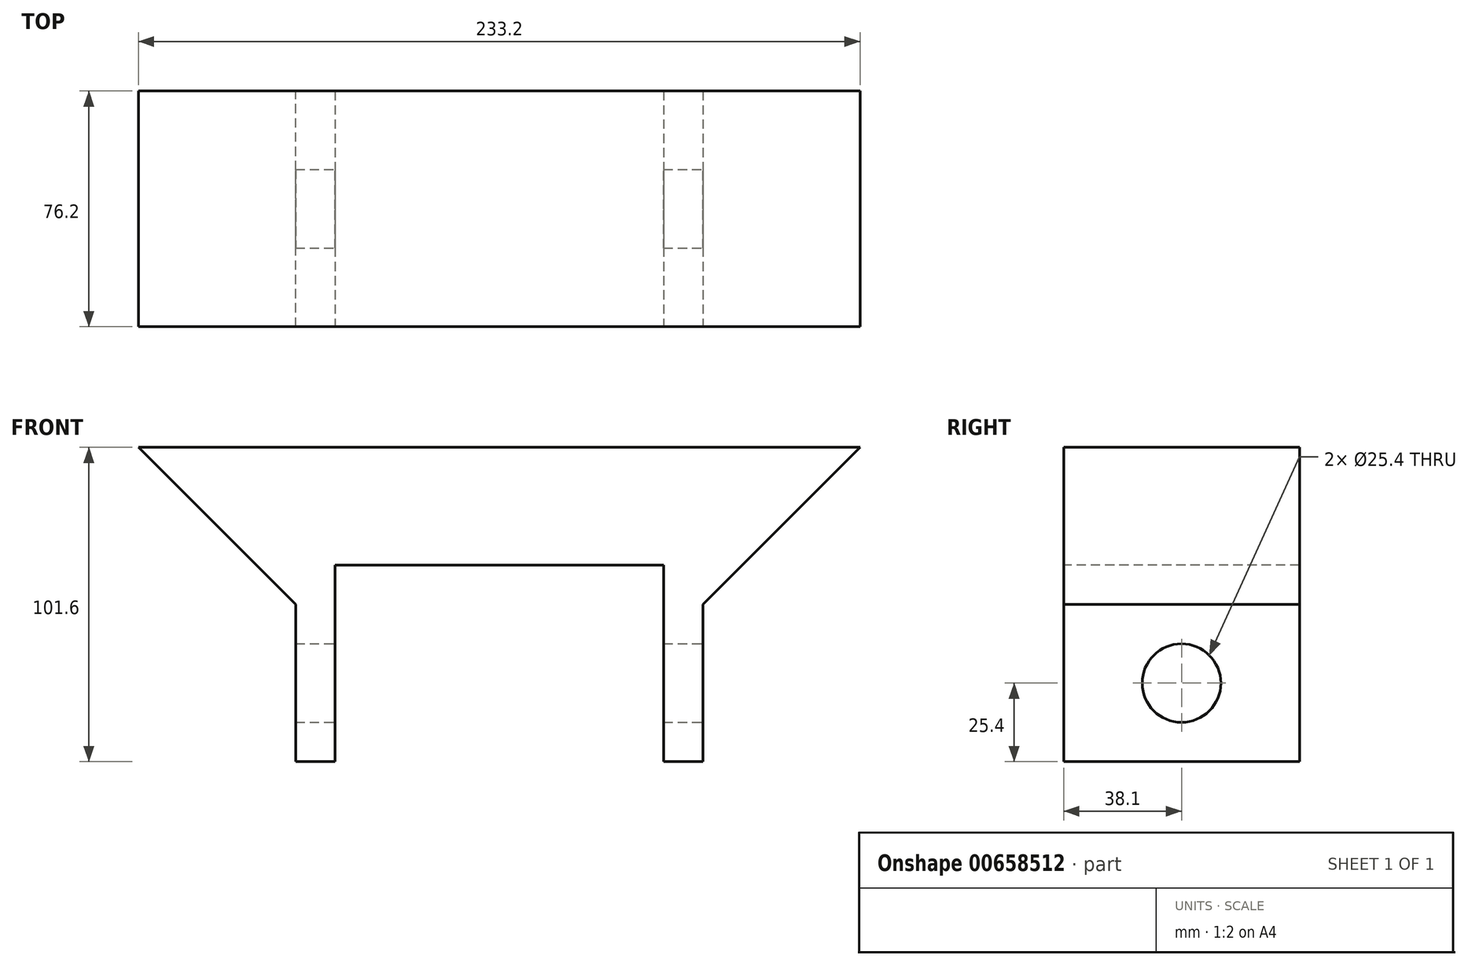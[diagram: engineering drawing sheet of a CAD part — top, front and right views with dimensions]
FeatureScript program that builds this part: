
annotation { "Feature Type Name" : "Feature", "Feature Type Description" : "" }
export const myFeature = defineFeature(function(context is Context, id is Id, definition is map)
    precondition{}
    {
        {
            var Q0;
            Q0=qCreatedBy(makeId("Top.planeOp"),FACE);
            var sketch = newSketch(context, id + "F0", { "sketchPlane" : qUnion([Q0])});
            skLineSegment(sketch, "E0.bottom", {"start": v(0, 0) * mm, "end": v(284, 0) * mm});
            skLineSegment(sketch, "E0.top", {"start": v(0, 76.2) * mm, "end": v(284, 76.2) * mm});
            skLineSegment(sketch, "E0.left", {"start": v(0, 0) * mm, "end": v(0, 76.2) * mm});
            skLineSegment(sketch, "E0.right", {"start": v(284, 0) * mm, "end": v(284, 76.2) * mm});
            skSolve(sketch);
        }
        {
            var Q0;
            Q0=makeQuery(id+"F0.imprint","IMPRINT",FACE,{"disambiguationData":[TD([[makeQuery(id+"F0.imprint","IMPRINT",EDGE,{"derivedFrom":sQuery(id+"F0.wireOp",EDGE,"E0.bottom")}),1.0]])]});
            extrude(context, id + "F1", {"entities" : qUnion([Q0]), "oppositeDirection" : true, "depth" : 50.8 * mm, "offsetDistance" : 25.4 * mm});
        }
        {
            var Q0;
            Q0=makeQuery(id+"F1.opExtrude","CAP_EDGE",EDGE,{"disambiguationData":[OSD([sQuery(id+"F0.wireOp",EDGE,"E0.left")])],"isStart":false});
            var Q1;
            Q1=makeQuery(id+"F1.opExtrude","CAP_EDGE",EDGE,{"disambiguationData":[OSD([sQuery(id+"F0.wireOp",EDGE,"E0.right")])],"isStart":false});
            chamfer(context, id + "F2", {"entities" : qUnion([Q0, Q1]), "width" : 76.2 * mm, "tangentPropagation" : true});
        }
        {
            var Q0;
            Q0=makeQuery(id+"F1.opExtrude","CAP_FACE",FACE,{"disambiguationData":[OSD([sQuery(id+"F0.wireOp",EDGE,"E0.bottom"),sQuery(id+"F0.wireOp",EDGE,"E0.top"),sQuery(id+"F0.wireOp",EDGE,"E0.left"),sQuery(id+"F0.wireOp",EDGE,"E0.right")])],"isStart":false});
            extrude(context, id + "F3", {"entities" : qUnion([Q0]), "operationType" : NewBodyOperationType.ADD, "depth" : 50.8 * mm, "offsetDistance" : 25.4 * mm});
        }
        {
            var Q0;
            Q0=makeQuery(id+"F3.opExtrude","CAP_FACE",FACE,{"disambiguationData":[OSD([sQuery(id+"F0.wireOp",EDGE,"E0.bottom"),sQuery(id+"F0.wireOp",EDGE,"E0.top"),sQuery(id+"F0.wireOp",EDGE,"E0.left"),sQuery(id+"F0.wireOp",EDGE,"E0.right")])],"isStart":false});
            var sketch = newSketch(context, id + "F4", { "sketchPlane" : qUnion([Q0])});
            skLineSegment(sketch, "E1.bottom", {"start": v(88.9, -76.2) * mm, "end": v(195.1, -76.2) * mm});
            skLineSegment(sketch, "E1.top", {"start": v(88.9, 0) * mm, "end": v(195.1, 0) * mm});
            skLineSegment(sketch, "E1.left", {"start": v(88.9, -76.2) * mm, "end": v(88.9, 0) * mm});
            skLineSegment(sketch, "E1.right", {"start": v(195.1, -76.2) * mm, "end": v(195.1, 0) * mm});
            skSolve(sketch);
        }
        {
            var Q0;
            Q0=qSketchRegion(id+"F4",true);
            extrude(context, id + "F5", {"entities" : qUnion([Q0]), "operationType" : NewBodyOperationType.REMOVE, "oppositeDirection" : true, "depth" : 63.5 * mm, "offsetDistance" : 25.4 * mm});
        }
        {
            var Q0;
            {var subQ0=sQuery(id+"F0.wireOp",EDGE,"E0.right");var subQ1=sQuery(id+"F0.wireOp",EDGE,"E0.left");var subQ2=sQuery(id+"F0.wireOp",EDGE,"E0.top");var subQ3=sQuery(id+"F0.wireOp",EDGE,"E0.bottom");Q0=makeQuery(id+"F3.opExtrude","SWEPT_FACE",FACE,{"disambiguationData":[OSD([subQ3,subQ2,subQ1,subQ0]),TDD([makeQuery(id+"F2.opChamfer","BLEND_EDGE",EDGE,{"blendedFrom":[makeQuery(id+"F1.opExtrude","CAP_EDGE",EDGE,{"disambiguationData":[OSD([subQ0])],"isStart":false}),makeQuery(id+"F1.opExtrude","CAP_FACE",FACE,{"disambiguationData":[OSD([subQ3,subQ2,subQ1,subQ0])],"isStart":false})],"blendedInto":[makeQuery(id+"F1.opExtrude","CAP_FACE",FACE,{"disambiguationData":[OSD([subQ3,subQ2,subQ1,subQ0])],"isStart":false})]})])]});}
            var sketch = newSketch(context, id + "F6", { "sketchPlane" : qUnion([Q0])});
            skCircle(sketch, "E2", {"center": v(38.1, -76.2) * mm, "radius": 12.7 * mm});
            skSolve(sketch);
        }
        {
            var Q0;
            Q0=makeQuery(id+"F6.imprint","IMPRINT",FACE,{"disambiguationData":[TD([[makeQuery(id+"F6.imprint","IMPRINT",EDGE,{"derivedFrom":sQuery(id+"F6.wireOp",EDGE,"E2")}),1.0]])]});
            extrude(context, id + "F7", {"entities" : qUnion([Q0]), "operationType" : NewBodyOperationType.REMOVE, "endBound" : BoundingType.THROUGH_ALL, "oppositeDirection" : true, "depth" : 25.4 * mm, "offsetDistance" : 25.4 * mm});
        }
    });
